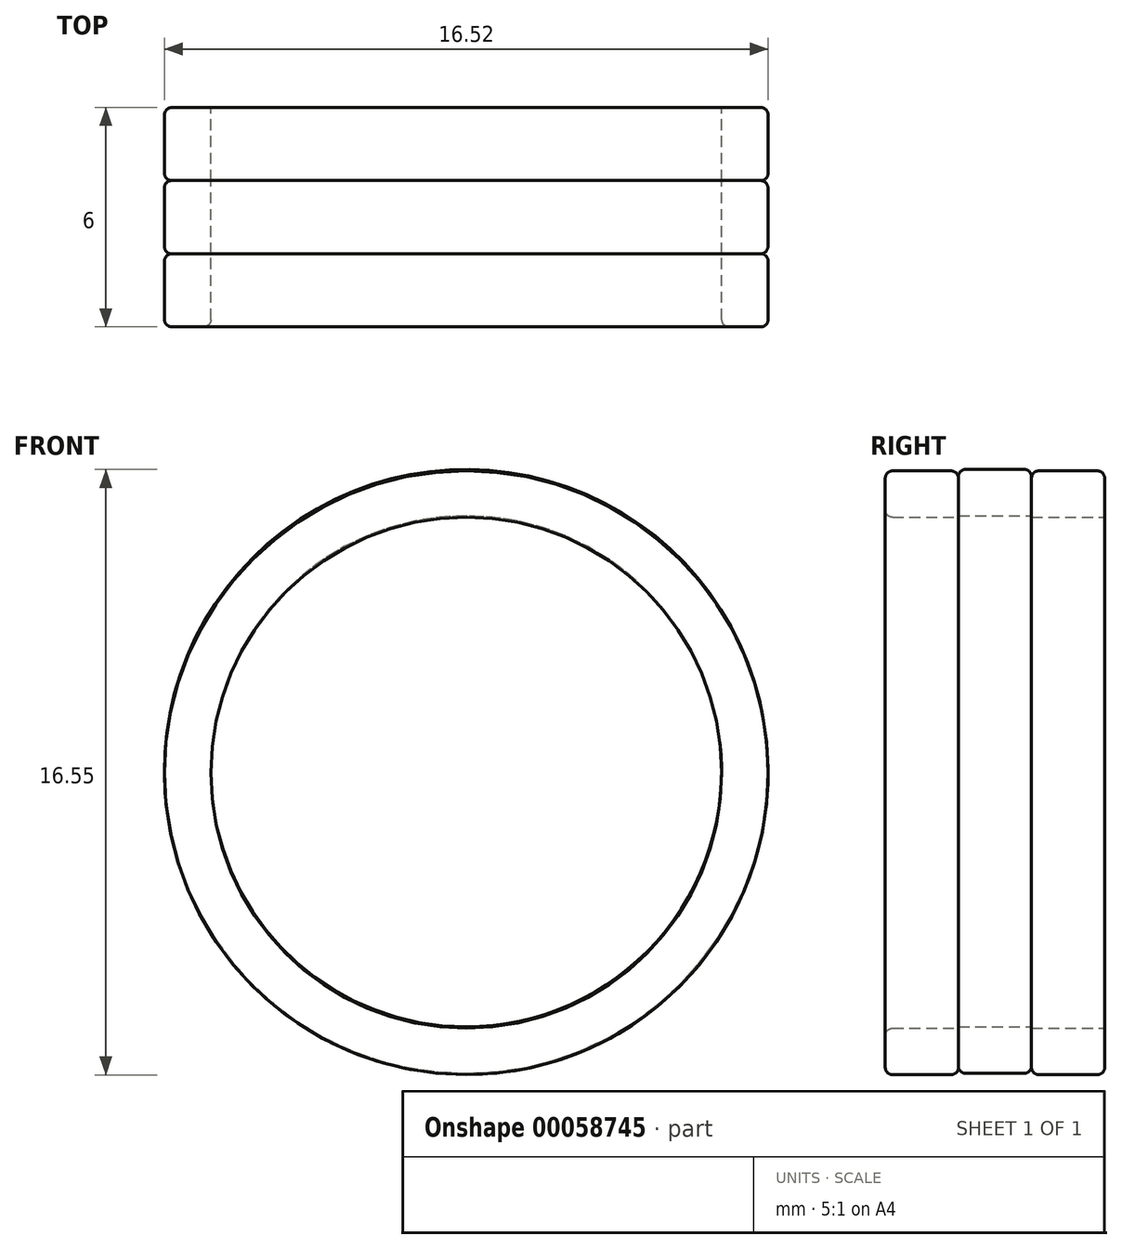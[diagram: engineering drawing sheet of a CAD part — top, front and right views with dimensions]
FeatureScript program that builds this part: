
annotation { "Feature Type Name" : "Feature", "Feature Type Description" : "" }
export const myFeature = defineFeature(function(context is Context, id is Id, definition is map)
    precondition{}
    {
        {
            var Q0;
            Q0=qCreatedBy(makeId("Right.planeOp"),FACE);
            var sketch = newSketch(context, id + "F0", { "sketchPlane" : qUnion([Q0])});
            skPoint(sketch, "E0", {"position": v(2, 0) * mm});
            skPoint(sketch, "E1", {"position": v(-2, 0) * mm});
            skSolve(sketch);
        }
        {
            var Q0;
            Q0=qCreatedBy(makeId("Front.planeOp"),FACE);
            cPlane(context, id + "F1", {"entities" : qUnion([Q0]), "cplaneType" : CPlaneType.OFFSET, "offset" : 2 * mm, "width" : 152.4 * mm, "height" : 152.4 * mm});
        }
        {
            var Q0;
            Q0=qCreatedBy(makeId("Front.planeOp"),FACE);
            cPlane(context, id + "F2", {"entities" : qUnion([Q0]), "cplaneType" : CPlaneType.OFFSET, "offset" : 2 * mm, "oppositeDirection" : true, "width" : 152.4 * mm, "height" : 152.4 * mm});
        }
        {
            var Q0;
            Q0=qCreatedBy(id+"F2.planeOp",FACE);
            var sketch = newSketch(context, id + "F3", { "sketchPlane" : qUnion([Q0])});
            skCircle(sketch, "E2", {"center": v(0, 0) * mm, "radius": 8.26 * mm});
            skCircle(sketch, "E3", {"center": v(0, 0) * mm, "radius": 6.99 * mm});
            skSolve(sketch);
        }
        {
            var Q0;
            Q0=qCreatedBy(id+"F1.planeOp",FACE);
            var sketch = newSketch(context, id + "F4", { "sketchPlane" : qUnion([Q0])});
            skCircle(sketch, "E4", {"center": v(0, 0) * mm, "radius": 6.99 * mm});
            skCircle(sketch, "E5", {"center": v(0, 0) * mm, "radius": 8.25 * mm});
            skSolve(sketch);
        }
        {
            var Q0;
            Q0=qCreatedBy(makeId("Front.planeOp"),FACE);
            var sketch = newSketch(context, id + "F5", { "sketchPlane" : qUnion([Q0])});
            skCircle(sketch, "E6", {"center": v(0, 0.04) * mm, "radius": 6.99 * mm});
            skCircle(sketch, "E7", {"center": v(0, 0.04) * mm, "radius": 8.26 * mm});
            skSolve(sketch);
        }
        {
            var Q0;
            Q0=makeQuery(id+"F4.imprint","IMPRINT",FACE,{"disambiguationData":[TD([[makeQuery(id+"F4.imprint","IMPRINT",EDGE,{"derivedFrom":sQuery(id+"F4.wireOp",EDGE,"E4")}),-1.0]])]});
            var Q1;
            Q1=sQuery(id+"F4.wireOp",EDGE,"E5");
            var Q2;
            Q2=sQuery(id+"F4.wireOp",EDGE,"E4");
            extrude(context, id + "F6", {"entities" : qUnion([Q0]), "surfaceEntities" : qUnion([Q1, Q2]), "depth" : 2 * mm});
        }
        {
            var Q0;
            Q0=makeQuery(id+"F5.imprint","IMPRINT",FACE,{"disambiguationData":[TD([[makeQuery(id+"F5.imprint","IMPRINT",EDGE,{"derivedFrom":sQuery(id+"F5.wireOp",EDGE,"E6")}),-1.0]])]});
            var Q1;
            Q1=sQuery(id+"F5.wireOp",EDGE,"E7");
            extrude(context, id + "F7", {"entities" : qUnion([Q0]), "surfaceEntities" : qUnion([Q1]), "depth" : 2 * mm});
        }
        {
            var Q0;
            Q0=makeQuery(id+"F3.imprint","IMPRINT",FACE,{"disambiguationData":[TD([[makeQuery(id+"F3.imprint","IMPRINT",EDGE,{"derivedFrom":sQuery(id+"F3.wireOp",EDGE,"E2")}),1.0]])]});
            var Q1;
            Q1=sQuery(id+"F3.wireOp",EDGE,"E3");
            var Q2;
            Q2=sQuery(id+"F3.wireOp",EDGE,"E2");
            extrude(context, id + "F8", {"entities" : qUnion([Q0]), "surfaceEntities" : qUnion([Q1, Q2]), "depth" : 2 * mm});
        }
        {
            var Q0;
            Q0=makeQuery(id+"F8.opExtrude","CAP_EDGE",EDGE,{"disambiguationData":[OSD([sQuery(id+"F3.wireOp",EDGE,"E2")])],"isStart":true});
            var Q1;
            Q1=makeQuery(id+"F7.opExtrude","CAP_EDGE",EDGE,{"disambiguationData":[OSD([sQuery(id+"F5.wireOp",EDGE,"E7")])],"isStart":true});
            fillet(context, id + "F9", {"entities" : qUnion([Q0, Q1]), "radius" : 0.2 * mm, "tangentPropagation" : true, "allowEdgeOverflow" : false});
        }
        {
            var Q0;
            Q0=makeQuery(id+"F8.opExtrude","CAP_EDGE",EDGE,{"disambiguationData":[OSD([sQuery(id+"F3.wireOp",EDGE,"E2")])],"isStart":false});
            var Q1;
            Q1=makeQuery(id+"F6.opExtrude","CAP_EDGE",EDGE,{"disambiguationData":[OSD([sQuery(id+"F4.wireOp",EDGE,"E5")])],"isStart":true});
            var Q2;
            Q2=makeQuery(id+"F6.opExtrude","CAP_EDGE",EDGE,{"disambiguationData":[OSD([sQuery(id+"F4.wireOp",EDGE,"E4")])],"isStart":false});
            fillet(context, id + "F10", {"entities" : qUnion([Q0, Q1, Q2]), "radius" : .2 * mm, "tangentPropagation" : true, "allowEdgeOverflow" : false});
        }
        {
            var Q0;
            Q0=makeQuery(id+"F7.opExtrude","CAP_EDGE",EDGE,{"disambiguationData":[OSD([sQuery(id+"F5.wireOp",EDGE,"E7")])],"isStart":false});
            var Q1;
            Q1=makeQuery(id+"F6.opExtrude","CAP_EDGE",EDGE,{"disambiguationData":[OSD([sQuery(id+"F4.wireOp",EDGE,"E5")])],"isStart":false});
            fillet(context, id + "F11", {"entities" : qUnion([Q0, Q1]), "radius" : .2 * mm, "tangentPropagation" : true, "allowEdgeOverflow" : false});
        }
    });
